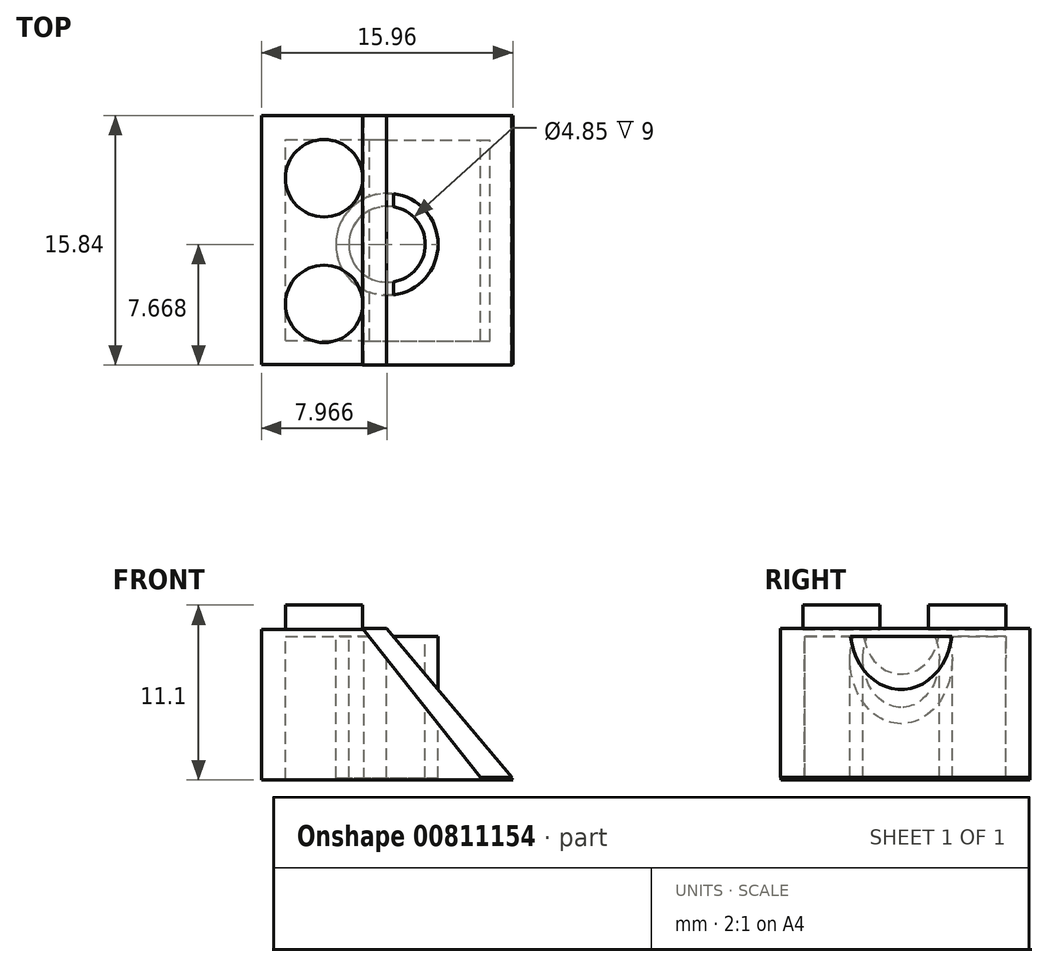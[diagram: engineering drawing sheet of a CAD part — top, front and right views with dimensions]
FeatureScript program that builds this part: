
annotation { "Feature Type Name" : "Feature", "Feature Type Description" : "" }
export const myFeature = defineFeature(function(context is Context, id is Id, definition is map)
    precondition{}
    {
        {
            var Q0;
            Q0=qCreatedBy(makeId("Front.planeOp"),FACE);
            var sketch = newSketch(context, id + "F0", { "sketchPlane" : qUnion([Q0])});
            skLineSegment(sketch, "E0.bottom", {"start": v(-10.9, 0.47) * mm, "end": v(-2.97, 0.47) * mm});
            skLineSegment(sketch, "E0.left", {"start": v(-10.9, 0.47) * mm, "end": v(-10.9, -9.1) * mm});
            skLineSegment(sketch, "E1", {"start": v(5.05, -9.1) * mm, "end": v(-2.97, 0.47) * mm});
            skLineSegment(sketch, "E2", {"start": v(-10.9, -9.1) * mm, "end": v(5.05, -9.1) * mm});
            skSolve(sketch);
        }
        {
            var Q0;
            Q0 = qSketchRegion(id + "F0", true);
            extrude(context, id + "F1", {"entities" : qUnion([Q0]), "depth" : 15.8 * mm, "offsetDistance" : 25 * mm});
        }
        {
            var Q0;
            Q0=qCreatedBy(makeId("Top.planeOp"),FACE);
            var sketch = newSketch(context, id + "F2", { "sketchPlane" : qUnion([Q0])});
            skCircle(sketch, "E3", {"center": v(-6.94, -3.98) * mm, "radius": 2.46 * mm});
            skCircle(sketch, "E4", {"center": v(-6.94, -11.96) * mm, "radius": 2.46 * mm});
            skSolve(sketch);
        }
        {
            var Q0;
            Q0 = qSketchRegion(id + "F2", true);
            extrude(context, id + "F3", {"entities" : qUnion([Q0]), "operationType" : NewBodyOperationType.ADD, "depth" : 2 * mm, "offsetDistance" : 25 * mm});
        }
        {
            var Q0;
            Q0=qCreatedBy(makeId("Top.planeOp"),FACE);
            var sketch = newSketch(context, id + "F4", { "sketchPlane" : qUnion([Q0])});
            skLineSegment(sketch, "E5.bottom", {"start": v(-9.38, -14.28) * mm, "end": v(-3.02, -14.28) * mm});
            skLineSegment(sketch, "E5.top", {"start": v(-9.38, -1.52) * mm, "end": v(-3.02, -1.52) * mm});
            skLineSegment(sketch, "E5.left", {"start": v(-9.38, -14.28) * mm, "end": v(-9.38, -1.52) * mm});
            skLineSegment(sketch, "E6", {"start": v(-3.02, -14.28) * mm, "end": v(-3.02, -1.52) * mm});
            skSolve(sketch);
        }
        {
            var Q0;
            Q0 = qSketchRegion(id + "F4", true);
            extrude(context, id + "F5", {"entities" : qUnion([Q0]), "operationType" : NewBodyOperationType.REMOVE, "oppositeDirection" : true, "depth" : 10 * mm, "offsetDistance" : 25 * mm});
        }
        {
            var Q0;
            Q0=qCreatedBy(makeId("Top.planeOp"),FACE);
            var sketch = newSketch(context, id + "F6", { "sketchPlane" : qUnion([Q0])});
            skLineSegment(sketch, "E7.bottom", {"start": v(-4.39, -14.3) * mm, "end": v(3.61, -14.3) * mm});
            skLineSegment(sketch, "E7.top", {"start": v(-4.39, -1.54) * mm, "end": v(3.61, -1.54) * mm});
            skLineSegment(sketch, "E7.left", {"start": v(-4.39, -14.3) * mm, "end": v(-4.39, -1.54) * mm});
            skLineSegment(sketch, "E7.right", {"start": v(3.61, -14.3) * mm, "end": v(3.61, -1.54) * mm});
            skSolve(sketch);
        }
        {
            var Q0;
            Q0 = qSketchRegion(id + "F6", true);
            extrude(context, id + "F7", {"entities" : qUnion([Q0]), "operationType" : NewBodyOperationType.REMOVE, "oppositeDirection" : true, "depth" : 10 * mm, "offsetDistance" : 25 * mm});
        }
        {
            var Q0;
            Q0=qCreatedBy(makeId("Front.planeOp"),FACE);
            var sketch = newSketch(context, id + "F8", { "sketchPlane" : qUnion([Q0])});
            skLineSegment(sketch, "E8", {"start": v(-2.97, 0.51) * mm, "end": v(5, -8.94) * mm});
            skLineSegment(sketch, "E9", {"start": v(5, -8.94) * mm, "end": v(2.99, -8.94) * mm});
            skLineSegment(sketch, "E10", {"start": v(2.99, -8.94) * mm, "end": v(-4.48, 0.51) * mm});
            skLineSegment(sketch, "E11", {"start": v(-4.48, 0.51) * mm, "end": v(-2.97, 0.51) * mm});
            skSolve(sketch);
        }
        {
            var Q0;
            Q0 = qSketchRegion(id + "F8", true);
            extrude(context, id + "F9", {"entities" : qUnion([Q0]), "operationType" : NewBodyOperationType.ADD, "depth" : 15.84 * mm, "offsetDistance" : 25 * mm});
        }
        {
            var Q0;
            Q0=qCreatedBy(makeId("Top.planeOp"),FACE);
            var sketch = newSketch(context, id + "F10", { "sketchPlane" : qUnion([Q0])});
            skCircle(sketch, "E12", {"center": v(-2.94, -8.17) * mm, "radius": 3.25 * mm});
            skCircle(sketch, "E13", {"center": v(-2.94, -8.17) * mm, "radius": 2.43 * mm});
            skSolve(sketch);
        }
        {
            var Q0;
            Q0 = qSketchRegion(id + "F10", true);
            extrude(context, id + "F11", {"entities" : qUnion([Q0]), "operationType" : NewBodyOperationType.ADD, "oppositeDirection" : true, "depth" : 9 * mm, "offsetDistance" : 25 * mm});
        }
    });
